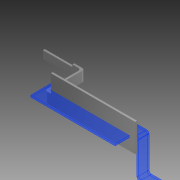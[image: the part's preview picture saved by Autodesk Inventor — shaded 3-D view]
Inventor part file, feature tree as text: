
AUTODESK INVENTOR PART (.ipt)
format: ipt  version: 2014 (Build 180170000, 170)  size: 123,904 bytes
history: native  units: in
note: dims shown in document units (in); Inventor stores cm internally (conversion verified against a paired STEP export)
features: extrude x2, sketch x2, reference x2, fillet x1
ambient origin geometry x8: Origin, YZ Plane, XZ Plane, XY Plane, X Axis, Y Axis, Z Axis, Center Point
bodies: Solid1 (feature_tree)
feature tree (7):
  extrude  "Extrusion1"  Depth=0.2677in
  extrude  "Extrusion2"  Depth=0.0039in
  fillet  "Fillet1"  Radius=0.0039in
  sketch  "Sketch1"  dims[d0=0.2323in d1=0.2677in]
  reference  "Reference1"
  reference  "Reference2"
  sketch  "Sketch2"  dims[d2=0.0787in d3=0.0in d4=0.0039in d5=0.0039in d6=0.0827in d7=0.0039in d8=0.005in d9=0.005in d10=0.0787in d11=0.0in d12=0.005in d13=0.0748in d14=0.0374in]
